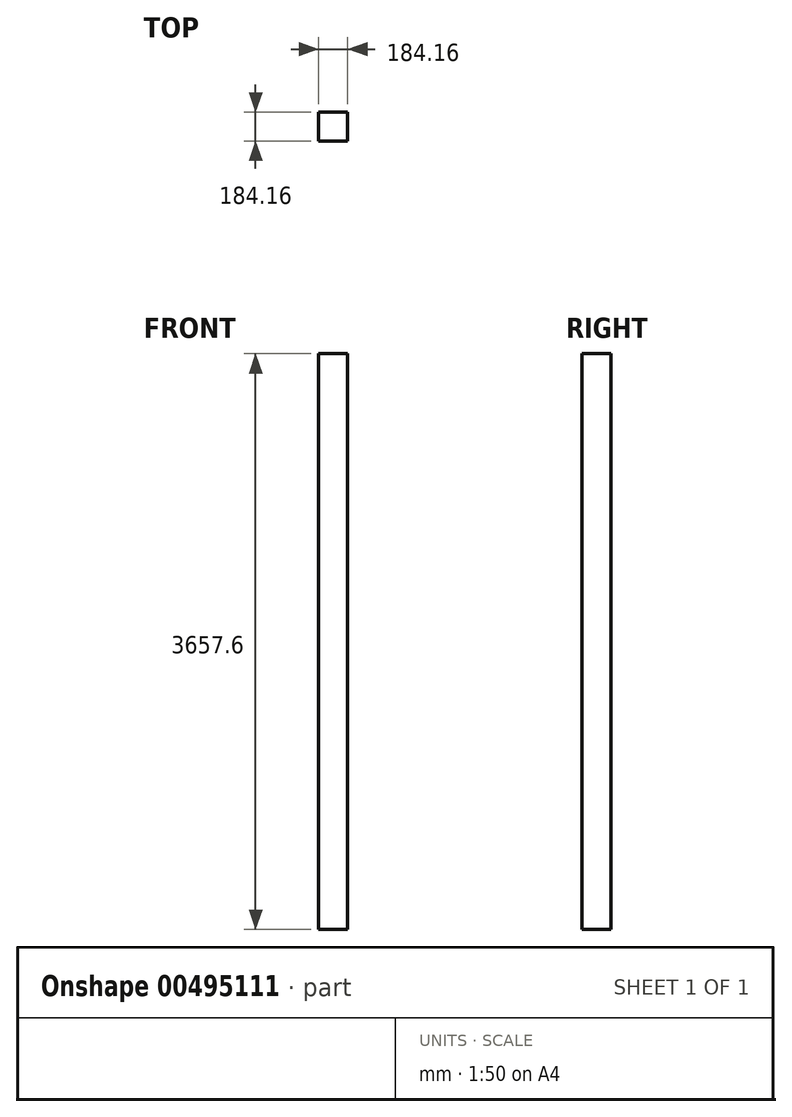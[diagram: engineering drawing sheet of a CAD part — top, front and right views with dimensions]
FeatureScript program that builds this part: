
annotation { "Feature Type Name" : "Feature", "Feature Type Description" : "" }
export const myFeature = defineFeature(function(context is Context, id is Id, definition is map)
    precondition{}
    {
        {
            var Q0;
            Q0=qCreatedBy(makeId("Top.planeOp"),FACE);
            var sketch = newSketch(context, id + "F0", { "sketchPlane" : qUnion([Q0])});
            skLineSegment(sketch, "E0.bottom", {"start": v(-92.07, 92.08) * mm, "end": v(92.08, 92.08) * mm});
            skLineSegment(sketch, "E0.top", {"start": v(-92.08, -92.08) * mm, "end": v(92.08, -92.08) * mm});
            skLineSegment(sketch, "E0.left", {"start": v(-92.07, 92.08) * mm, "end": v(-92.08, -92.08) * mm});
            skLineSegment(sketch, "E0.right", {"start": v(92.08, 92.08) * mm, "end": v(92.08, -92.08) * mm});
            skPoint(sketch, "E0.middle", {"position": v(0, 0) * mm});
            skSolve(sketch);
        }
        {
            var Q0;
            Q0 = qSketchRegion(id + "F0", true);
            extrude(context, id + "F1", {"entities" : qUnion([Q0]), "depth" : 3657.6 * mm});
        }
    });
